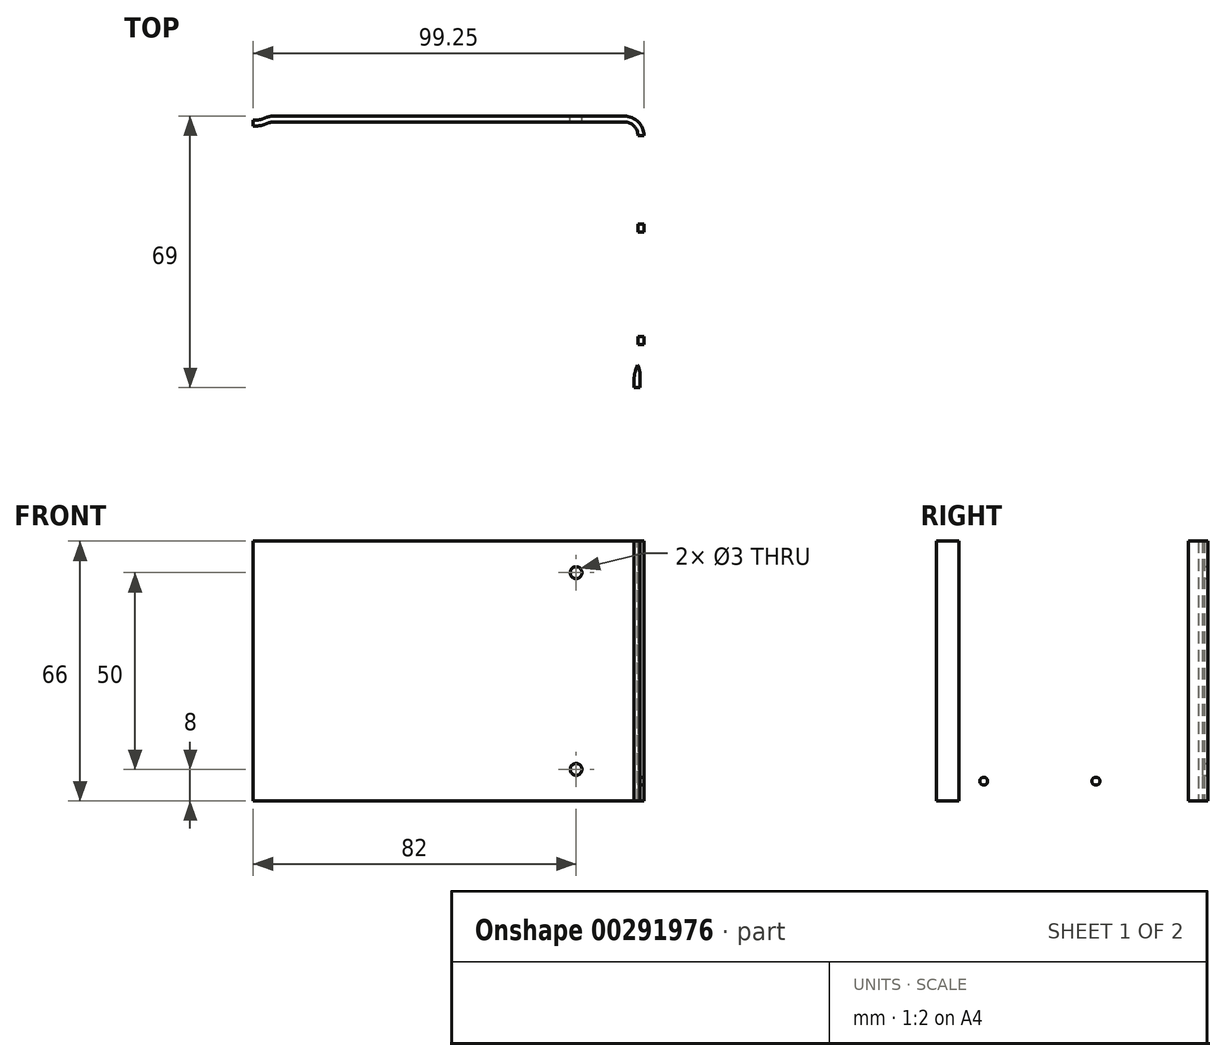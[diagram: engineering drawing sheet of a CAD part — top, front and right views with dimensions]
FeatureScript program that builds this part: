
annotation { "Feature Type Name" : "Feature", "Feature Type Description" : "" }
export const myFeature = defineFeature(function(context is Context, id is Id, definition is map)
    precondition{}
    {
        {
            var Q0;
            Q0=qCreatedBy(makeId("Top.planeOp"),FACE);
            var sketch = newSketch(context, id + "F0", { "sketchPlane" : qUnion([Q0])});
            skLineSegment(sketch, "E0", {"start": v(54.5, -24.99) * mm, "end": v(54.5, 33) * mm});
            skLineSegment(sketch, "E1", {"start": v(-46, 33) * mm, "end": v(-46, 0) * mm});
            skLineSegment(sketch, "E2.0", {"start": v(-47.5, 33) * mm, "end": v(-47.5, 0) * mm});
            skLineSegment(sketch, "E2.3", {"start": v(56, -25.25) * mm, "end": v(56, 33) * mm});
            skLineSegment(sketch, "E2.4", {"start": v(51, 38) * mm, "end": v(-42.5, 38) * mm});
            skLineSegment(sketch, "E3", {"start": v(-46, 0) * mm, "end": v(-47.5, 0) * mm});
            skPoint(sketch, "E4.visualSharp", {"position": v(54.5, 36.5) * mm});
            skArc(sketch, "E4.filletArc", {"start": v(54.5, 33) * mm, "mid": v(53.47, 35.47) * mm, "end": v(51, 36.5) * mm});
            skPoint(sketch, "E5.visualSharp", {"position": v(-46, 36.5) * mm});
            skArc(sketch, "E5.filletArc", {"start": v(-42.5, 36.5) * mm, "mid": v(-44.97, 35.47) * mm, "end": v(-46, 33) * mm});
            skPoint(sketch, "E6.visualSharp", {"position": v(56, 38) * mm});
            skArc(sketch, "E6.filletArc", {"start": v(56, 33) * mm, "mid": v(54.54, 36.54) * mm, "end": v(51, 38) * mm});
            skPoint(sketch, "E7.visualSharp", {"position": v(-47.5, 38) * mm});
            skArc(sketch, "E7.filletArc", {"start": v(-42.5, 38) * mm, "mid": v(-46.04, 36.54) * mm, "end": v(-47.5, 33) * mm});
            skLineSegment(sketch, "E8", {"start": v(54.5, 0) * mm, "end": v(-12.48, 0) * mm, "construction": true});
            skLineSegment(sketch, "E9", {"start": v(0, 36.5) * mm, "end": v(0, -15.2) * mm, "construction": true});
            skLineSegment(sketch, "E10", {"start": v(-42.5, 36.5) * mm, "end": v(51, 36.5) * mm});
            skLineSegment(sketch, "E11", {"start": v(55, -31) * mm, "end": v(55, -28) * mm});
            skLineSegment(sketch, "E12", {"start": v(55, -28) * mm, "end": v(56, -25.25) * mm});
            skLineSegment(sketch, "E13", {"start": v(55, -31) * mm, "end": v(53.5, -31) * mm});
            skLineSegment(sketch, "E14", {"start": v(53.5, -31) * mm, "end": v(53.5, -27.74) * mm});
            skLineSegment(sketch, "E15", {"start": v(53.5, -27.74) * mm, "end": v(54.5, -24.99) * mm});
            skSolve(sketch);
        }
        {
            var Q0;
            Q0=qSketchRegion(id+"F0",true);
            var Q1;
            Q1=qSketchRegion(id+"F4",true);
            extrude(context, id + "F1", {"entities" : qUnion([Q0, Q1]), "depth" : 66 * mm});
        }
        {
            var Q0;
            Q0=makeQuery(id+"F1.opExtrude","SWEPT_FACE",FACE,{"disambiguationData":[OSD([sQuery(id+"F0.wireOp",EDGE,"E2.4")])]});
            var sketch = newSketch(context, id + "F2", { "sketchPlane" : qUnion([Q0])});
            skCircle(sketch, "E16", {"center": v(-38.75, 58) * mm, "radius": 1.5 * mm});
            skLineSegment(sketch, "E17", {"start": v(-38.75, 58) * mm, "end": v(-38.75, 8) * mm, "construction": true});
            skLineSegment(sketch, "E18", {"start": v(-38.75, 8) * mm, "end": v(38.75, 8) * mm, "construction": true});
            skLineSegment(sketch, "E19", {"start": v(38.75, 8) * mm, "end": v(38.75, 58) * mm, "construction": true});
            skLineSegment(sketch, "E20", {"start": v(38.75, 58) * mm, "end": v(-38.75, 58) * mm, "construction": true});
            skCircle(sketch, "E21", {"center": v(-38.75, 8) * mm, "radius": 1.5 * mm});
            skCircle(sketch, "E22", {"center": v(38.75, 8) * mm, "radius": 1.5 * mm});
            skCircle(sketch, "E23", {"center": v(38.75, 58) * mm, "radius": 1.5 * mm});
            skLineSegment(sketch, "E24", {"start": v(0, 0) * mm, "end": v(0, 116) * mm, "construction": true});
            skPoint(sketch, "E24.endSnap0", {"position": v(0, 0) * mm});
            skPoint(sketch, "E25", {"position": v(0, 58) * mm});
            skCircle(sketch, "E26", {"center": v(38.75, 49.63) * mm, "radius": 1.5 * mm});
            skCircle(sketch, "E27", {"center": v(38.75, 16.38) * mm, "radius": 1.5 * mm});
            skLineSegment(sketch, "E28", {"start": v(36, 33) * mm, "end": v(27.19, 33) * mm, "construction": true});
            skSolve(sketch);
        }
        {
            var Q0;
            Q0=makeQuery(id+"F2.imprint","IMPRINT",FACE,{"disambiguationData":[TD([[makeQuery(id+"F2.imprint","IMPRINT",EDGE,{"derivedFrom":sQuery(id+"F2.wireOp",EDGE,"E16")}),1.0]])]});
            var Q1;
            Q1=makeQuery(id+"F2.imprint","IMPRINT",FACE,{"disambiguationData":[TD([[makeQuery(id+"F2.imprint","IMPRINT",EDGE,{"derivedFrom":sQuery(id+"F2.wireOp",EDGE,"E21")}),1.0]])]});
            extrude(context, id + "F3", {"entities" : qUnion([Q0, Q1]), "operationType" : NewBodyOperationType.REMOVE, "oppositeDirection" : true, "depth" : 25 * mm});
        }
        {
            var Q0;
            Q0=makeQuery(id+"F1.opExtrude","SWEPT_FACE",FACE,{"disambiguationData":[OSD([sQuery(id+"F0.wireOp",EDGE,"E2.3")])]});
            var sketch = newSketch(context, id + "F4", { "sketchPlane" : qUnion([Q0])});
            skLineSegment(sketch, "E29.bottom", {"start": v(-21, 58) * mm, "end": v(-17, 58) * mm});
            skLineSegment(sketch, "E29.top", {"start": v(-21, 8) * mm, "end": v(-17, 8) * mm});
            skLineSegment(sketch, "E29.left", {"start": v(-24, 55) * mm, "end": v(-24, 11) * mm});
            skLineSegment(sketch, "E29.right", {"start": v(-14, 55) * mm, "end": v(-14, 11) * mm});
            skLineSegment(sketch, "E30.bottom", {"start": v(-5, 58) * mm, "end": v(24, 58) * mm});
            skLineSegment(sketch, "E30.top", {"start": v(-5, 8) * mm, "end": v(24, 8) * mm});
            skLineSegment(sketch, "E30.left", {"start": v(-8, 55) * mm, "end": v(-8, 11) * mm});
            skLineSegment(sketch, "E30.right", {"start": v(27, 55) * mm, "end": v(27, 11) * mm});
            skLineSegment(sketch, "E31", {"start": v(-14, 58) * mm, "end": v(-8, 58) * mm, "construction": true});
            skLineSegment(sketch, "E32", {"start": v(-14, 8) * mm, "end": v(-8, 8) * mm, "construction": true});
            skPoint(sketch, "E33.visualSharp", {"position": v(-24, 58) * mm});
            skArc(sketch, "E33.filletArc", {"start": v(-21, 58) * mm, "mid": v(-23.12, 57.12) * mm, "end": v(-24, 55) * mm});
            skPoint(sketch, "E34.visualSharp", {"position": v(-14, 58) * mm});
            skArc(sketch, "E34.filletArc", {"start": v(-14, 55) * mm, "mid": v(-14.88, 57.12) * mm, "end": v(-17, 58) * mm});
            skPoint(sketch, "E35.visualSharp", {"position": v(-24, 8) * mm});
            skArc(sketch, "E35.filletArc", {"start": v(-24, 11) * mm, "mid": v(-23.12, 8.88) * mm, "end": v(-21, 8) * mm});
            skPoint(sketch, "E36.visualSharp", {"position": v(-14, 8) * mm});
            skArc(sketch, "E36.filletArc", {"start": v(-17, 8) * mm, "mid": v(-14.88, 8.88) * mm, "end": v(-14, 11) * mm});
            skPoint(sketch, "E37.visualSharp", {"position": v(-8, 8) * mm});
            skArc(sketch, "E37.filletArc", {"start": v(-8, 11) * mm, "mid": v(-7.12, 8.88) * mm, "end": v(-5, 8) * mm});
            skPoint(sketch, "E38.visualSharp", {"position": v(27, 8) * mm});
            skArc(sketch, "E38.filletArc", {"start": v(24, 8) * mm, "mid": v(26.12, 8.88) * mm, "end": v(27, 11) * mm});
            skPoint(sketch, "E39.visualSharp", {"position": v(27, 58) * mm});
            skArc(sketch, "E39.filletArc", {"start": v(27, 55) * mm, "mid": v(26.12, 57.12) * mm, "end": v(24, 58) * mm});
            skPoint(sketch, "E40.visualSharp", {"position": v(-8, 58) * mm});
            skArc(sketch, "E40.filletArc", {"start": v(-5, 58) * mm, "mid": v(-7.12, 57.12) * mm, "end": v(-8, 55) * mm});
            skCircle(sketch, "E41", {"center": v(-19, 61) * mm, "radius": 1 * mm});
            skLineSegment(sketch, "E42", {"start": v(-24, 33) * mm, "end": v(27, 33) * mm, "construction": true});
            skLineSegment(sketch, "E43", {"start": v(-19, 58) * mm, "end": v(-19, 8) * mm, "construction": true});
            skPoint(sketch, "E43.endSnap0", {"position": v(-19, 8) * mm});
            skLineSegment(sketch, "E44", {"start": v(9.5, 8) * mm, "end": v(9.5, 58) * mm, "construction": true});
            skCircle(sketch, "E45", {"center": v(9.5, 61) * mm, "radius": 1 * mm});
            skCircle(sketch, "E46.MirrorC", {"center": v(-19, 5) * mm, "radius": 1 * mm});
            skCircle(sketch, "E47.MirrorC", {"center": v(9.5, 5) * mm, "radius": 1 * mm});
            skSolve(sketch);
        }
        {
            var Q0;
            Q0=makeQuery(id+"F4.imprint","IMPRINT",FACE,{"disambiguationData":[TD([[makeQuery(id+"F4.imprint","IMPRINT",EDGE,{"derivedFrom":sQuery(id+"F4.wireOp",EDGE,"E29.bottom")}),-1.0]])]});
            var Q1;
            Q1=makeQuery(id+"F4.imprint","IMPRINT",FACE,{"disambiguationData":[TD([[makeQuery(id+"F4.imprint","IMPRINT",EDGE,{"derivedFrom":sQuery(id+"F4.wireOp",EDGE,"E30.bottom")}),-1.0]])]});
            var Q2;
            Q2=makeQuery(id+"F4.imprint","IMPRINT",FACE,{"disambiguationData":[TD([[makeQuery(id+"F4.imprint","IMPRINT",EDGE,{"derivedFrom":sQuery(id+"F4.wireOp",EDGE,"E29.bottom")}),-1.0]])]});
            var Q3;
            Q3=makeQuery(id+"F4.imprint","IMPRINT",FACE,{"disambiguationData":[TD([[makeQuery(id+"F4.imprint","IMPRINT",EDGE,{"derivedFrom":sQuery(id+"F4.wireOp",EDGE,"E30.bottom")}),-1.0]])]});
            var Q4;
            Q4=makeQuery(id+"F4.imprint","IMPRINT",FACE,{"disambiguationData":[TD([[makeQuery(id+"F4.imprint","IMPRINT",EDGE,{"derivedFrom":sQuery(id+"F4.wireOp",EDGE,"E41")}),1.0]])]});
            var Q5;
            Q5=makeQuery(id+"F4.imprint","IMPRINT",FACE,{"disambiguationData":[TD([[makeQuery(id+"F4.imprint","IMPRINT",EDGE,{"derivedFrom":sQuery(id+"F4.wireOp",EDGE,"E45")}),1.0]])]});
            var Q6;
            Q6=makeQuery(id+"F4.imprint","IMPRINT",FACE,{"disambiguationData":[TD([[makeQuery(id+"F4.imprint","IMPRINT",EDGE,{"derivedFrom":sQuery(id+"F4.wireOp",EDGE,"E47.MirrorC")}),-1.0]])]});
            var Q7;
            Q7=makeQuery(id+"F4.imprint","IMPRINT",FACE,{"disambiguationData":[TD([[makeQuery(id+"F4.imprint","IMPRINT",EDGE,{"derivedFrom":sQuery(id+"F4.wireOp",EDGE,"E46.MirrorC")}),-1.0]])]});
            extrude(context, id + "F5", {"entities" : qUnion([Q0, Q1, Q2, Q3, Q4, Q5, Q6, Q7]), "operationType" : NewBodyOperationType.REMOVE, "oppositeDirection" : true, "depth" : 25 * mm});
        }
        {
            var Q0;
            Q0=makeQuery(id+"F1.opExtrude","SWEPT_EDGE",EDGE,{"disambiguationData":[OSD([sQuery(id+"F0.wireOp",EDGE,"E11"),sQuery(id+"F0.wireOp",EDGE,"E12")])]});
            var Q1;
            Q1=makeQuery(id+"F1.opExtrude","SWEPT_EDGE",EDGE,{"disambiguationData":[OSD([sQuery(id+"F0.wireOp",EDGE,"E0"),sQuery(id+"F0.wireOp",EDGE,"E15")])]});
            fillet(context, id + "F6", {"entities" : qUnion([Q0, Q1]), "radius" : 5 * mm, "tangentPropagation" : true, "allowEdgeOverflow" : false});
        }
        {
            var Q0;
            Q0=makeQuery(id+"F1.opExtrude","SWEPT_EDGE",EDGE,{"disambiguationData":[OSD([sQuery(id+"F0.wireOp",EDGE,"E2.3"),sQuery(id+"F0.wireOp",EDGE,"E12")])]});
            var Q1;
            Q1=makeQuery(id+"F1.opExtrude","SWEPT_EDGE",EDGE,{"disambiguationData":[OSD([sQuery(id+"F0.wireOp",EDGE,"E14"),sQuery(id+"F0.wireOp",EDGE,"E15")])]});
            fillet(context, id + "F7", {"entities" : qUnion([Q0, Q1]), "radius" : 6.5 * mm, "tangentPropagation" : true, "allowEdgeOverflow" : false});
        }
        {
            var Q0;
            Q0=qCreatedBy(makeId("Top.planeOp"),FACE);
            var sketch = newSketch(context, id + "F8", { "sketchPlane" : qUnion([Q0])});
            skLineSegment(sketch, "E48.bottom", {"start": v(-49.5, 43) * mm, "end": v(-38, 43) * mm});
            skLineSegment(sketch, "E48.top", {"start": v(-49.5, -5) * mm, "end": v(-38, -5) * mm});
            skLineSegment(sketch, "E48.left", {"start": v(-49.5, 43) * mm, "end": v(-49.5, -5) * mm});
            skLineSegment(sketch, "E48.right", {"start": v(-38, 43) * mm, "end": v(-38, -5) * mm});
            skSolve(sketch);
        }
        {
            var Q0;
            Q0=makeQuery(id+"F8.imprint","IMPRINT",FACE,{"disambiguationData":[TD([[makeQuery(id+"F8.imprint","IMPRINT",EDGE,{"derivedFrom":sQuery(id+"F8.wireOp",EDGE,"E48.bottom")}),-1.0]])]});
            extrude(context, id + "F9", {"entities" : qUnion([Q0]), "operationType" : NewBodyOperationType.REMOVE, "depth" : 100 * mm});
        }
        {
            var Q0;
            Q0=qCreatedBy(makeId("Top.planeOp"),FACE);
            var sketch = newSketch(context, id + "F10", { "sketchPlane" : qUnion([Q0])});
            skLineSegment(sketch, "E49", {"start": v(-43.25, 35.5) * mm, "end": v(-42.25, 35.5) * mm});
            skLineSegment(sketch, "E50", {"start": v(-40.54, 35.8) * mm, "end": v(-39.2, 36.29) * mm});
            skLineSegment(sketch, "E51", {"start": v(-39.71, 37.7) * mm, "end": v(-41.05, 37.21) * mm});
            skLineSegment(sketch, "E52", {"start": v(-42.25, 37) * mm, "end": v(-43.25, 37) * mm});
            skLineSegment(sketch, "E53", {"start": v(-43.25, 37) * mm, "end": v(-43.25, 35.5) * mm});
            skPoint(sketch, "E54.visualSharp", {"position": v(-41.63, 37) * mm});
            skArc(sketch, "E54.filletArc", {"start": v(-42.25, 37) * mm, "mid": v(-41.64, 37.05) * mm, "end": v(-41.05, 37.21) * mm});
            skPoint(sketch, "E55.visualSharp", {"position": v(-41.36, 35.5) * mm});
            skArc(sketch, "E55.filletArc", {"start": v(-42.25, 35.5) * mm, "mid": v(-41.38, 35.58) * mm, "end": v(-40.54, 35.8) * mm});
            skLineSegment(sketch, "E56", {"start": v(-38, 36.5) * mm, "end": v(-38, 36.5) * mm});
            skLineSegment(sketch, "E57", {"start": v(-38, 36.5) * mm, "end": v(-38, 38) * mm});
            skLineSegment(sketch, "E58", {"start": v(-38, 38) * mm, "end": v(-38, 38) * mm});
            skPoint(sketch, "E59.visualSharp", {"position": v(-38.88, 38) * mm});
            skArc(sketch, "E59.filletArc", {"start": v(-38, 38) * mm, "mid": v(-38.87, 37.92) * mm, "end": v(-39.71, 37.7) * mm});
            skPoint(sketch, "E60.visualSharp", {"position": v(-38.62, 36.5) * mm});
            skArc(sketch, "E60.filletArc", {"start": v(-38, 36.5) * mm, "mid": v(-38.6, 36.45) * mm, "end": v(-39.2, 36.29) * mm});
            skSolve(sketch);
        }
        {
            var Q0;
            Q0=makeQuery(id+"F10.imprint","IMPRINT",FACE,{"disambiguationData":[TD([[makeQuery(id+"F10.imprint","IMPRINT",EDGE,{"derivedFrom":sQuery(id+"F10.wireOp",EDGE,"E49")}),1.0]])]});
            extrude(context, id + "F11", {"entities" : qUnion([Q0]), "operationType" : NewBodyOperationType.ADD, "depth" : 66 * mm});
        }
    });
